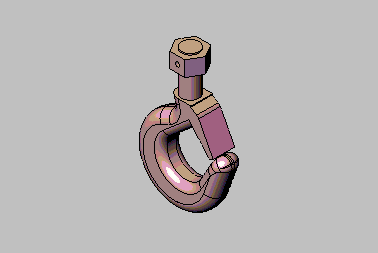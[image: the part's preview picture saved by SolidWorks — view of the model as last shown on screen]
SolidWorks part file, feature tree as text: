
SOLIDWORKS PART (.sldprt)
format: sldprt  version: not decoded by parser v0  size: 1,422,848 bytes
history: native  units: mm
features: plane x5, sketch x4, extrude x3, fillet x2, material x1, mirror x1, cut_extrude x1 (+10 scaffold rows collapsed)
feature tree (27):
  scaffold x10  (default folders/planes/origin — collapsed)
  material  "Material <not specified>"
  plane  "Plane1"  Offset=0mm
  plane  "Plane2"  Offset=0mm
  plane  "Plane3"  Offset=0mm
  sketch  "Sketch1"
  extrude  "Extrude1"  Depth=11.90625mm
  fillet  "Fillet1"  Radius=10.31875mm
  fillet  "Fillet2"  Radius=7.14375mm
  mirror  "Mirror1"
  sketch  "Sketch2"  dims[D1=19.05mm]
  extrude  "Extrude2"  Depth=44.45mm
  plane  "Plane4"  Offset=0mm
  plane  "Plane5"  Offset=26.19375mm
  sketch  "Sketch3"  dims[D1=28.575mm D2=28.575mm]
  extrude  "Extrude3"  Depth=16.891mm
  sketch  "Sketch4"  dims[D1=4.7625mm D2=8.4455mm]
  cut_extrude  "Cut-Extrude1"  [1 undecoded]
decode coverage: 8 of 11 modeling features carry decoded parameters
note: 1 parameter value undecoded
note: suppression state not decoded; provenance and decode notes live in map.json
